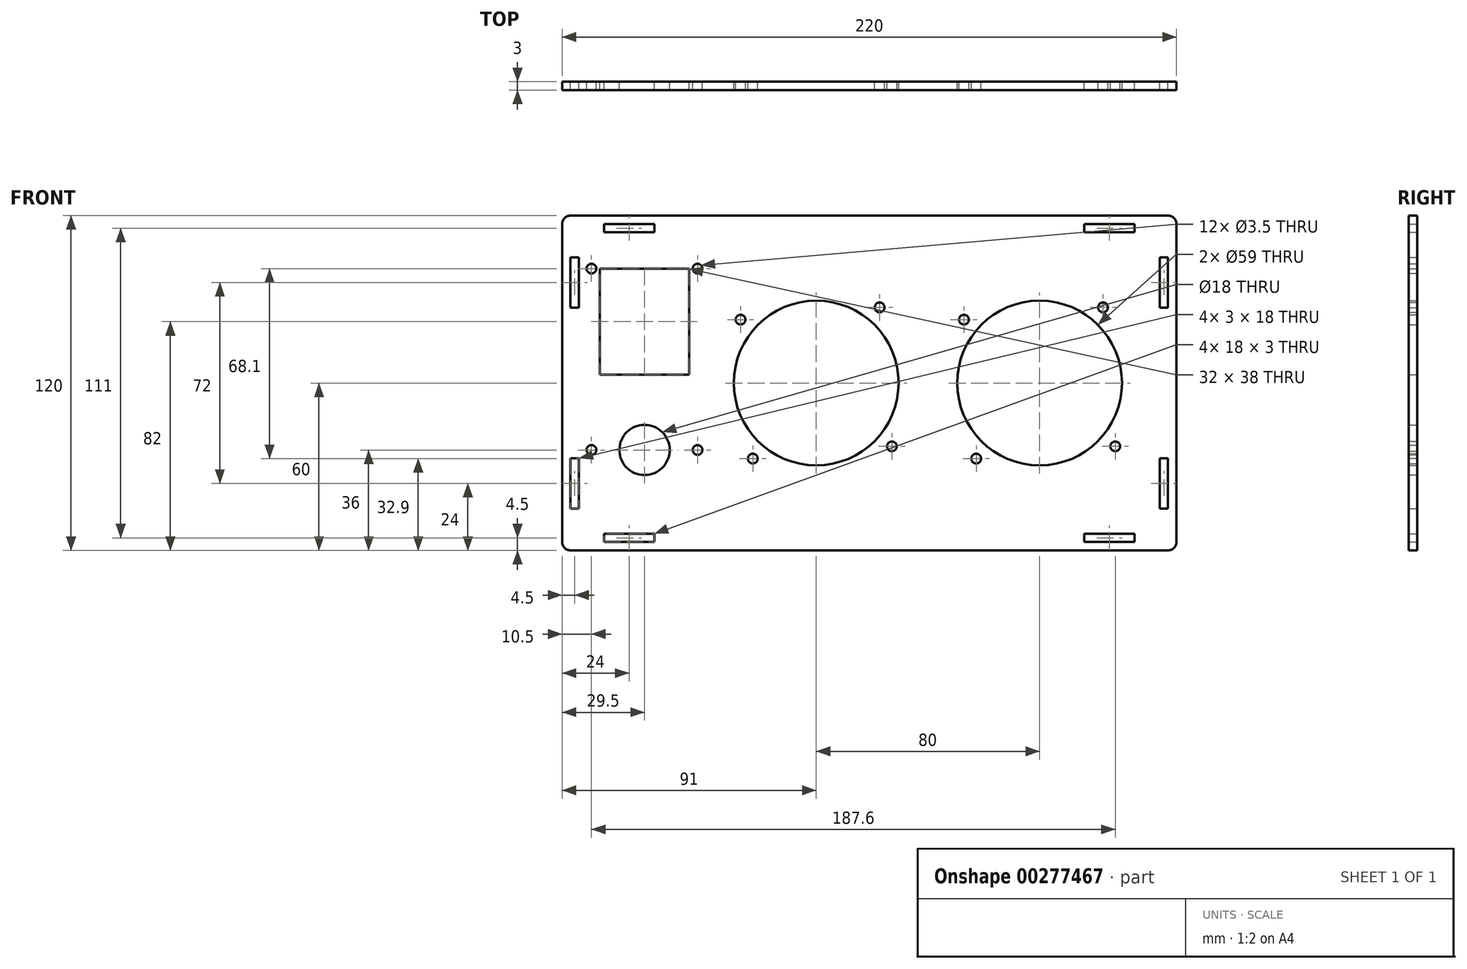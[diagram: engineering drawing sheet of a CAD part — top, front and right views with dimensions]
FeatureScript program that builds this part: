
annotation { "Feature Type Name" : "Feature", "Feature Type Description" : "" }
export const myFeature = defineFeature(function(context is Context, id is Id, definition is map)
    precondition{}
    {
        {
            var Q0;
            Q0=qCreatedBy(makeId("Front.planeOp"),FACE);
            var sketch = newSketch(context, id + "F0", { "sketchPlane" : qUnion([Q0])});
            skLineSegment(sketch, "E0.bottom", {"start": v(-107, 60) * mm, "end": v(107, 60) * mm});
            skLineSegment(sketch, "E0.top", {"start": v(-107, -60) * mm, "end": v(107, -60) * mm});
            skLineSegment(sketch, "E0.left", {"start": v(-110, 57) * mm, "end": v(-110, -57) * mm});
            skLineSegment(sketch, "E0.right", {"start": v(110, 57) * mm, "end": v(110, -57) * mm});
            skPoint(sketch, "E1.visualSharp", {"position": v(-110, 60) * mm});
            skArc(sketch, "E1.filletArc", {"start": v(-107, 60) * mm, "mid": v(-109.12, 59.12) * mm, "end": v(-110, 57) * mm});
            skPoint(sketch, "E2.visualSharp", {"position": v(110, 60) * mm});
            skArc(sketch, "E2.filletArc", {"start": v(110, 57) * mm, "mid": v(109.12, 59.12) * mm, "end": v(107, 60) * mm});
            skPoint(sketch, "E3.visualSharp", {"position": v(110, -60) * mm});
            skArc(sketch, "E3.filletArc", {"start": v(107, -60) * mm, "mid": v(109.12, -59.12) * mm, "end": v(110, -57) * mm});
            skPoint(sketch, "E4.visualSharp", {"position": v(-110, -60) * mm});
            skArc(sketch, "E4.filletArc", {"start": v(-110, -57) * mm, "mid": v(-109.12, -59.12) * mm, "end": v(-107, -60) * mm});
            skLineSegment(sketch, "E5.bottom", {"start": v(-95, 57) * mm, "end": v(-77, 57) * mm});
            skLineSegment(sketch, "E5.top", {"start": v(-95, 54) * mm, "end": v(-77, 54) * mm});
            skLineSegment(sketch, "E5.left", {"start": v(-95, 57) * mm, "end": v(-95, 54) * mm});
            skLineSegment(sketch, "E5.right", {"start": v(-77, 57) * mm, "end": v(-77, 54) * mm});
            skLineSegment(sketch, "E6.bottom", {"start": v(77, 57) * mm, "end": v(95, 57) * mm});
            skLineSegment(sketch, "E6.top", {"start": v(77, 54) * mm, "end": v(95, 54) * mm});
            skLineSegment(sketch, "E6.left", {"start": v(77, 57) * mm, "end": v(77, 54) * mm});
            skLineSegment(sketch, "E6.right", {"start": v(95, 57) * mm, "end": v(95, 54) * mm});
            skLineSegment(sketch, "E7.bottom", {"start": v(107, 45) * mm, "end": v(104, 45) * mm});
            skLineSegment(sketch, "E7.top", {"start": v(107, 27) * mm, "end": v(104, 27) * mm});
            skLineSegment(sketch, "E7.left", {"start": v(107, 45) * mm, "end": v(107, 27) * mm});
            skLineSegment(sketch, "E7.right", {"start": v(104, 45) * mm, "end": v(104, 27) * mm});
            skLineSegment(sketch, "E8.bottom", {"start": v(107, -27) * mm, "end": v(104, -27) * mm});
            skLineSegment(sketch, "E8.top", {"start": v(107, -45) * mm, "end": v(104, -45) * mm});
            skLineSegment(sketch, "E8.left", {"start": v(107, -27) * mm, "end": v(107, -45) * mm});
            skLineSegment(sketch, "E8.right", {"start": v(104, -27) * mm, "end": v(104, -45) * mm});
            skLineSegment(sketch, "E9.bottom", {"start": v(95, -57) * mm, "end": v(77, -57) * mm});
            skLineSegment(sketch, "E9.top", {"start": v(95, -54) * mm, "end": v(77, -54) * mm});
            skLineSegment(sketch, "E9.left", {"start": v(95, -57) * mm, "end": v(95, -54) * mm});
            skLineSegment(sketch, "E9.right", {"start": v(77, -57) * mm, "end": v(77, -54) * mm});
            skLineSegment(sketch, "E10.bottom", {"start": v(-77, -57) * mm, "end": v(-95, -57) * mm});
            skLineSegment(sketch, "E10.top", {"start": v(-77, -54) * mm, "end": v(-95, -54) * mm});
            skLineSegment(sketch, "E10.left", {"start": v(-77, -57) * mm, "end": v(-77, -54) * mm});
            skLineSegment(sketch, "E10.right", {"start": v(-95, -57) * mm, "end": v(-95, -54) * mm});
            skLineSegment(sketch, "E11.bottom", {"start": v(-104, -27) * mm, "end": v(-107, -27) * mm});
            skLineSegment(sketch, "E11.top", {"start": v(-104, -45) * mm, "end": v(-107, -45) * mm});
            skLineSegment(sketch, "E11.left", {"start": v(-104, -45) * mm, "end": v(-104, -27) * mm});
            skLineSegment(sketch, "E11.right", {"start": v(-107, -45) * mm, "end": v(-107, -27) * mm});
            skLineSegment(sketch, "E12.bottom", {"start": v(-104, 27) * mm, "end": v(-107, 27) * mm});
            skLineSegment(sketch, "E12.top", {"start": v(-104, 45) * mm, "end": v(-107, 45) * mm});
            skLineSegment(sketch, "E12.left", {"start": v(-104, 27) * mm, "end": v(-104, 45) * mm});
            skLineSegment(sketch, "E12.right", {"start": v(-107, 27) * mm, "end": v(-107, 45) * mm});
            skCircle(sketch, "E13", {"center": v(61, 0) * mm, "radius": 29.5 * mm});
            skCircle(sketch, "E14", {"center": v(83.7, 27.1) * mm, "radius": 1.75 * mm});
            skCircle(sketch, "E15", {"center": v(33.9, 22.7) * mm, "radius": 1.75 * mm});
            skCircle(sketch, "E16", {"center": v(38.3, -27.1) * mm, "radius": 1.75 * mm});
            skCircle(sketch, "E17", {"center": v(88.1, -22.7) * mm, "radius": 1.75 * mm});
            skLineSegment(sketch, "E18", {"start": v(-110, 0) * mm, "end": v(110, 0) * mm, "construction": true});
            skCircle(sketch, "E19", {"center": v(-80.5, -24) * mm, "radius": 9 * mm});
            skLineSegment(sketch, "E20", {"start": v(23, -5.98) * mm, "end": v(23, -18.14) * mm, "construction": true});
            skLineSegment(sketch, "E21.bottom", {"start": v(-96.5, 41) * mm, "end": v(-64.5, 41) * mm});
            skLineSegment(sketch, "E21.top", {"start": v(-96.5, 3) * mm, "end": v(-64.5, 3) * mm});
            skLineSegment(sketch, "E21.left", {"start": v(-96.5, 41) * mm, "end": v(-96.5, 3) * mm});
            skLineSegment(sketch, "E21.right", {"start": v(-64.5, 41) * mm, "end": v(-64.5, 3) * mm});
            skLineSegment(sketch, "E22", {"start": v(-80.5, -24) * mm, "end": v(-80.5, -20.92) * mm, "construction": true});
            skCircle(sketch, "E23", {"center": v(-99.5, 41) * mm, "radius": 1.75 * mm});
            skCircle(sketch, "E24", {"center": v(-61.5, 41) * mm, "radius": 1.75 * mm});
            skCircle(sketch, "E25", {"center": v(-99.5, -24) * mm, "radius": 1.75 * mm});
            skCircle(sketch, "E26", {"center": v(-61.5, -24) * mm, "radius": 1.75 * mm});
            skCircle(sketch, "E27", {"center": v(-19, 0) * mm, "radius": 29.5 * mm});
            skCircle(sketch, "E28", {"center": v(3.7, 27.1) * mm, "radius": 1.75 * mm});
            skCircle(sketch, "E29", {"center": v(-46.1, 22.7) * mm, "radius": 1.75 * mm});
            skCircle(sketch, "E30", {"center": v(-41.7, -27.1) * mm, "radius": 1.75 * mm});
            skCircle(sketch, "E31", {"center": v(8.1, -22.7) * mm, "radius": 1.75 * mm});
            skLineSegment(sketch, "E32", {"start": v(-57, 7.34) * mm, "end": v(-57, -27.64) * mm, "construction": true});
            skSolve(sketch);
        }
        {
            var Q0;
            Q0=makeQuery(id+"F0.imprint","IMPRINT",FACE,{"disambiguationData":[TD([[makeQuery(id+"F0.imprint","IMPRINT",EDGE,{"derivedFrom":sQuery(id+"F0.wireOp",EDGE,"E0.bottom")}),-1.0]])]});
            extrude(context, id + "F1", {"entities" : qUnion([Q0]), "depth" : 3 * mm});
        }
    });
